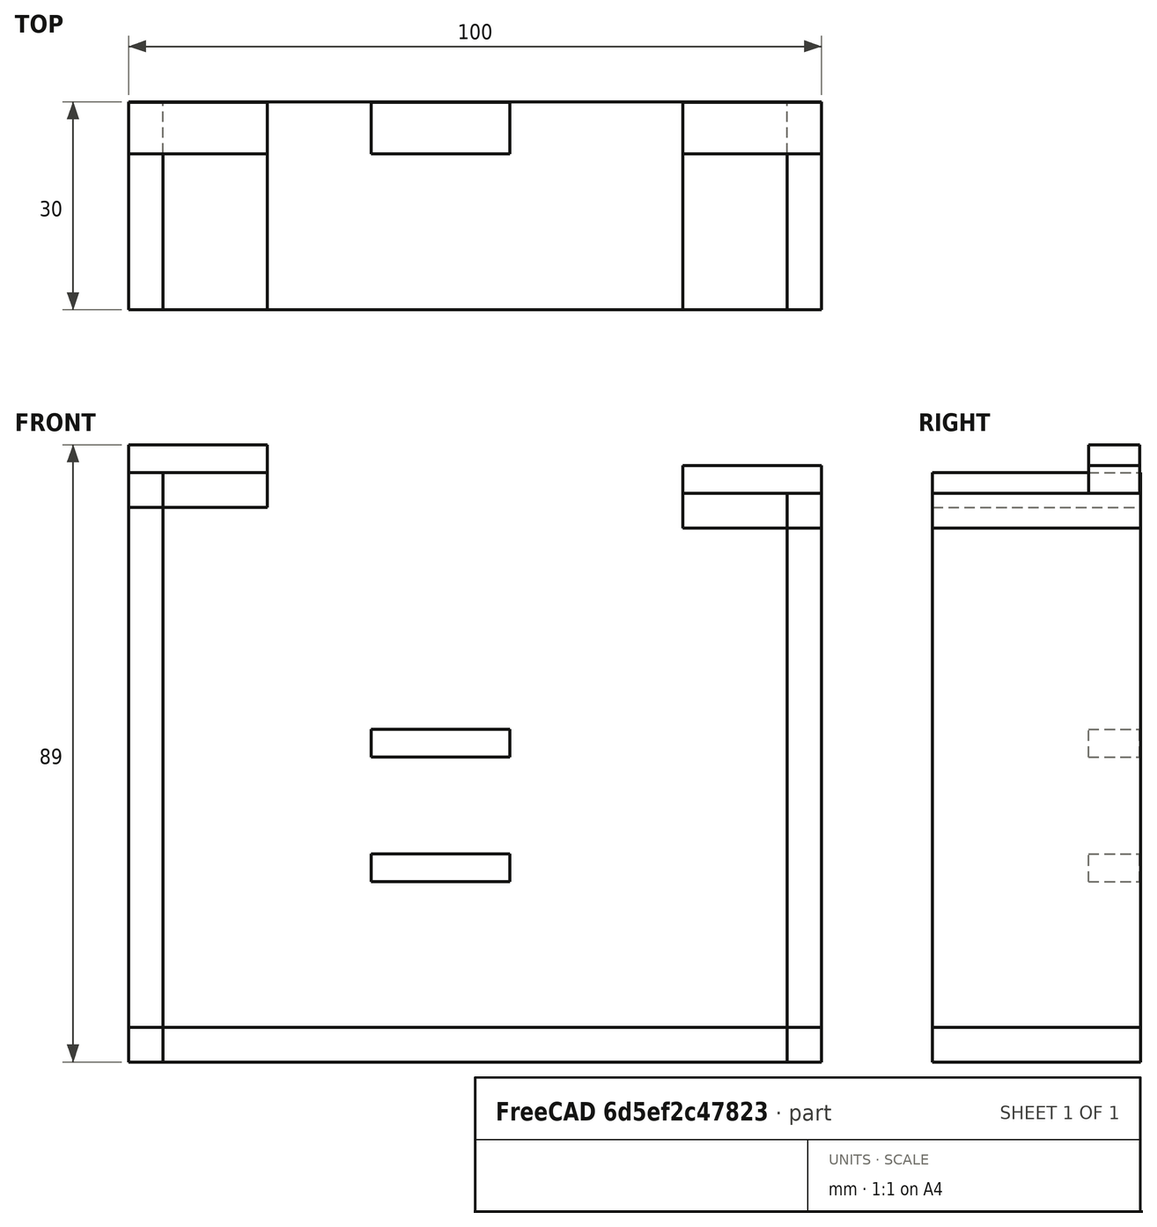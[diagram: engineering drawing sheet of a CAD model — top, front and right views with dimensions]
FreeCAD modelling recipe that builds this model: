
FCSTD DOCUMENT  (FreeCAD 0.15R4671 (Git))
Label: yoke2
License: All rights reserved
LicenseURL: http://en.wikipedia.org/wiki/All_rights_reserved
objects: Part::Box×9
note: 9 computed .brp shape members not serialized (recipe doc carries the construction recipe); baked Part::Feature solids carry a one-line shape summary decoded from their .brp

FEATURE [Part::Box] Box  label="Base"
  Height = 5
  Length = 100
  Width = 30
FEATURE [Part::Box] Box001  label="side reciever"
  Height = 85
  Length = 5
  Width = 30
FEATURE [Part::Box] Box002  label="side laser"
  Height = 82
  Length = 5
  Placement = pos=(95,0,0) rot=(0,0,1;0rad)
  Width = 30
FEATURE [Part::Box] Box003  label="platform laser"
  Height = 5
  Length = 20
  Placement = pos=(80,0,77) rot=(0,0,1;0rad)
  Width = 30
FEATURE [Part::Box] Box004  label="platform reciever"
  Height = 5
  Length = 20
  Placement = pos=(0,0,80) rot=(0,0,1;0rad)
  Width = 30
FEATURE [Part::Box] Box006  label="reciever case 002"
  Height = 4
  Length = 20
  Placement = pos=(0,22.5,85) rot=(0,0,1;0rad)
  Width = 7.4
FEATURE [Part::Box] Box008  label="laser case 002"
  Height = 4
  Length = 20
  Placement = pos=(80,22.5,82) rot=(0,0,1;0rad)
  Width = 7.4
FEATURE [Part::Box] Box009  label="reciever case 001"
  Height = 4
  Length = 20
  Placement = pos=(35,22.5,26) rot=(0,0,1;0rad)
  Width = 7.4
FEATURE [Part::Box] Box010  label="laser case 001"
  Height = 4
  Length = 20
  Placement = pos=(35,22.5,44) rot=(0,0,1;0rad)
  Width = 7.4
